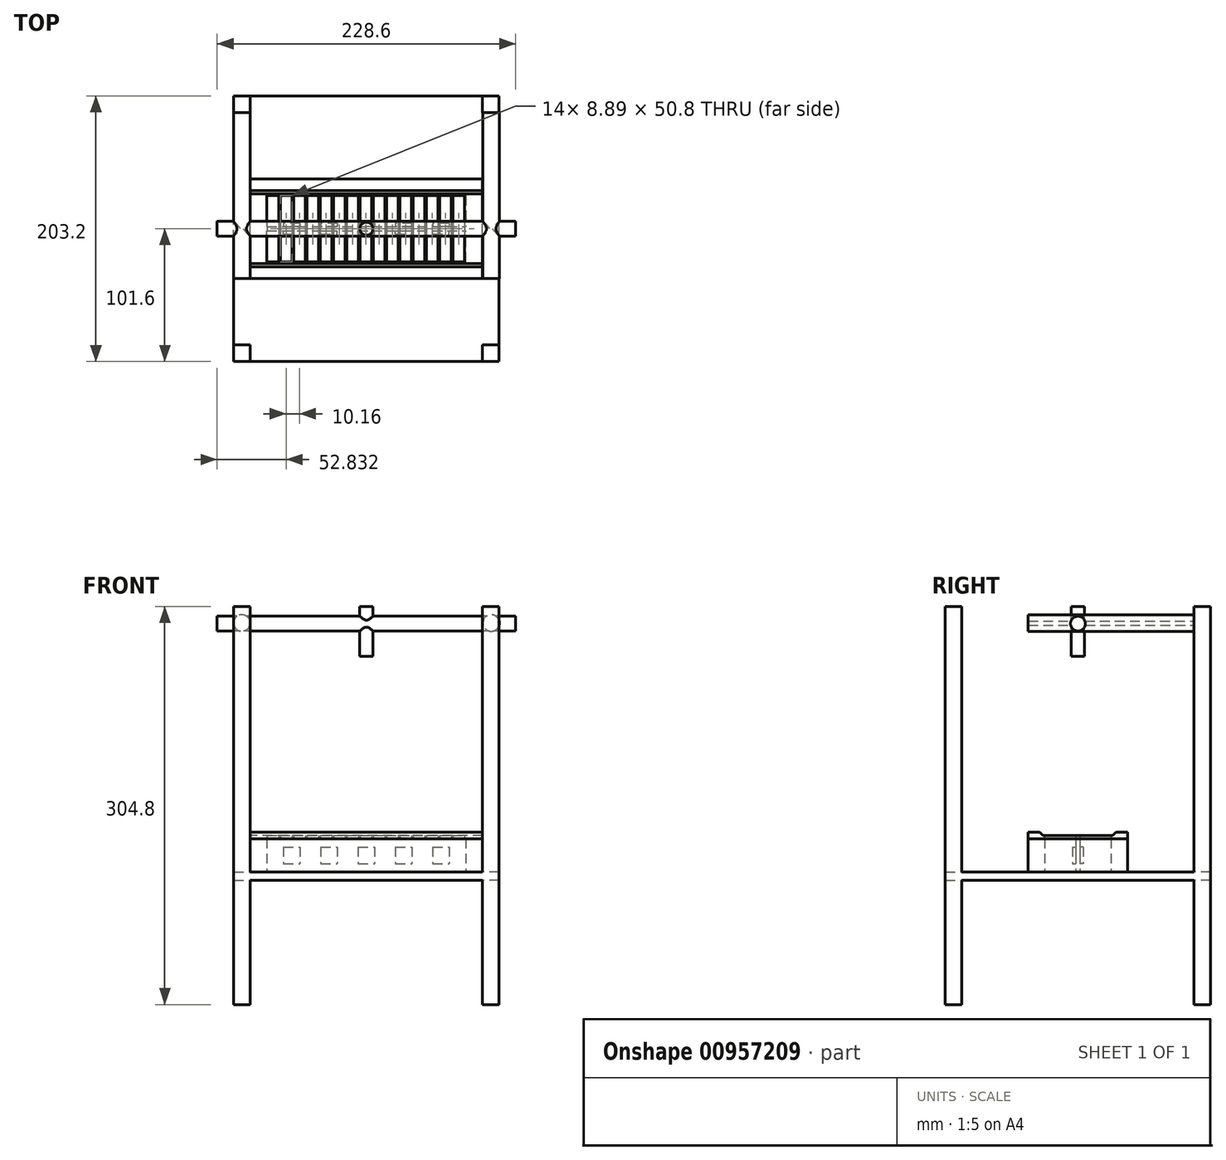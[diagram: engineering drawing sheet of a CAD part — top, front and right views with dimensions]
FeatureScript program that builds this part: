
annotation { "Feature Type Name" : "Feature", "Feature Type Description" : "" }
export const myFeature = defineFeature(function(context is Context, id is Id, definition is map)
    precondition{}
    {
        {
            var Q0;
            Q0=qCreatedBy(makeId("Top.planeOp"),FACE);
            var sketch = newSketch(context, id + "F0", { "sketchPlane" : qUnion([Q0])});
            skLineSegment(sketch, "E0.bottom", {"start": v(88.9, -38.1) * mm, "end": v(-88.9, -38.1) * mm});
            skLineSegment(sketch, "E0.top", {"start": v(88.9, 38.1) * mm, "end": v(-88.9, 38.1) * mm});
            skLineSegment(sketch, "E0.left", {"start": v(88.9, -38.1) * mm, "end": v(88.9, 38.1) * mm});
            skLineSegment(sketch, "E0.right", {"start": v(-88.9, -38.1) * mm, "end": v(-88.9, 38.1) * mm});
            skPoint(sketch, "E0.middle", {"position": v(0, 0) * mm});
            skLineSegment(sketch, "E1.bottom", {"start": v(-76.2, 25.4) * mm, "end": v(76.2, 25.4) * mm});
            skLineSegment(sketch, "E1.top", {"start": v(-76.2, 1.59) * mm, "end": v(76.2, 1.59) * mm});
            skLineSegment(sketch, "E1.left", {"start": v(-76.2, 25.4) * mm, "end": v(-76.2, 1.59) * mm});
            skLineSegment(sketch, "E1.right", {"start": v(76.2, 25.4) * mm, "end": v(76.2, 1.59) * mm});
            skLineSegment(sketch, "E2.bottom", {"start": v(-76.2, -25.4) * mm, "end": v(76.2, -25.4) * mm});
            skLineSegment(sketch, "E2.top", {"start": v(-76.2, -1.59) * mm, "end": v(76.2, -1.59) * mm});
            skLineSegment(sketch, "E2.left", {"start": v(-76.2, -25.4) * mm, "end": v(-76.2, -1.59) * mm});
            skLineSegment(sketch, "E2.right", {"start": v(76.2, -25.4) * mm, "end": v(76.2, -1.59) * mm});
            skSolve(sketch);
        }
        {
            var Q0;
            Q0=makeQuery(id+"F0.imprint","IMPRINT",FACE,{"disambiguationData":[TD([[makeQuery(id+"F0.imprint","IMPRINT",EDGE,{"derivedFrom":sQuery(id+"F0.wireOp",EDGE,"E0.bottom")}),-1.0]])]});
            extrude(context, id + "F1", {"entities" : qUnion([Q0]), "depth" : 25.4 * mm, "offsetDistance" : 25.4 * mm});
        }
        {
            var Q0;
            Q0=makeQuery(id+"F1.opExtrude","CAP_FACE",FACE,{"disambiguationData":[OSD([sQuery(id+"F0.wireOp",EDGE,"E0.bottom"),sQuery(id+"F0.wireOp",EDGE,"E0.top"),sQuery(id+"F0.wireOp",EDGE,"E0.left"),sQuery(id+"F0.wireOp",EDGE,"E0.right"),sQuery(id+"F0.wireOp",EDGE,"E1.bottom"),sQuery(id+"F0.wireOp",EDGE,"E1.top"),sQuery(id+"F0.wireOp",EDGE,"E1.left"),sQuery(id+"F0.wireOp",EDGE,"E1.right"),sQuery(id+"F0.wireOp",EDGE,"E2.bottom"),sQuery(id+"F0.wireOp",EDGE,"E2.top"),sQuery(id+"F0.wireOp",EDGE,"E2.left"),sQuery(id+"F0.wireOp",EDGE,"E2.right")])],"isStart":false});
            var sketch = newSketch(context, id + "F2", { "sketchPlane" : qUnion([Q0])});
            skLineSegment(sketch, "E3.bottom", {"start": v(-88.9, 38.1) * mm, "end": v(88.9, 38.1) * mm});
            skLineSegment(sketch, "E3.top", {"start": v(-88.9, -38.1) * mm, "end": v(88.9, -38.1) * mm});
            skLineSegment(sketch, "E3.left", {"start": v(-88.9, 38.1) * mm, "end": v(-88.9, -38.1) * mm});
            skLineSegment(sketch, "E3.right", {"start": v(88.9, 38.1) * mm, "end": v(88.9, -38.1) * mm});
            skLineSegment(sketch, "E4.bottom", {"start": v(-76.07, 25.4) * mm, "end": v(-67.18, 25.4) * mm});
            skLineSegment(sketch, "E4.top", {"start": v(-76.07, -25.4) * mm, "end": v(-67.18, -25.4) * mm});
            skLineSegment(sketch, "E4.left", {"start": v(-76.07, 25.4) * mm, "end": v(-76.07, -25.4) * mm});
            skLineSegment(sketch, "E4.right", {"start": v(-67.18, 25.4) * mm, "end": v(-67.18, -25.4) * mm});
            skLineSegment(sketch, "E5.bottom", {"start": v(-65.91, 25.4) * mm, "end": v(-57.02, 25.4) * mm});
            skLineSegment(sketch, "E5.top", {"start": v(-65.91, -25.4) * mm, "end": v(-57.02, -25.4) * mm});
            skLineSegment(sketch, "E5.left", {"start": v(-65.91, 25.4) * mm, "end": v(-65.91, -25.4) * mm});
            skLineSegment(sketch, "E5.right", {"start": v(-57.02, 25.4) * mm, "end": v(-57.02, -25.4) * mm});
            skLineSegment(sketch, "E6.bottom", {"start": v(-55.75, 25.4) * mm, "end": v(-46.86, 25.4) * mm});
            skLineSegment(sketch, "E6.top", {"start": v(-55.75, -25.4) * mm, "end": v(-46.86, -25.4) * mm});
            skLineSegment(sketch, "E6.left", {"start": v(-55.75, 25.4) * mm, "end": v(-55.75, -25.4) * mm});
            skLineSegment(sketch, "E6.right", {"start": v(-46.86, 25.4) * mm, "end": v(-46.86, -25.4) * mm});
            skLineSegment(sketch, "E7.bottom", {"start": v(-45.6, 25.4) * mm, "end": v(-36.7, 25.4) * mm});
            skLineSegment(sketch, "E7.top", {"start": v(-45.6, -25.4) * mm, "end": v(-36.7, -25.4) * mm});
            skLineSegment(sketch, "E7.left", {"start": v(-45.6, 25.4) * mm, "end": v(-45.6, -25.4) * mm});
            skLineSegment(sketch, "E7.right", {"start": v(-36.7, 25.4) * mm, "end": v(-36.7, -25.4) * mm});
            skLineSegment(sketch, "E8.bottom", {"start": v(-35.43, 25.4) * mm, "end": v(-26.54, 25.4) * mm});
            skLineSegment(sketch, "E8.top", {"start": v(-35.43, -25.4) * mm, "end": v(-26.54, -25.4) * mm});
            skLineSegment(sketch, "E8.left", {"start": v(-35.43, 25.4) * mm, "end": v(-35.43, -25.4) * mm});
            skLineSegment(sketch, "E8.right", {"start": v(-26.54, 25.4) * mm, "end": v(-26.54, -25.4) * mm});
            skLineSegment(sketch, "E9.bottom", {"start": v(-25.27, 25.4) * mm, "end": v(-16.38, 25.4) * mm});
            skLineSegment(sketch, "E9.top", {"start": v(-25.27, -25.4) * mm, "end": v(-16.38, -25.4) * mm});
            skLineSegment(sketch, "E9.left", {"start": v(-25.27, 25.4) * mm, "end": v(-25.27, -25.4) * mm});
            skLineSegment(sketch, "E9.right", {"start": v(-16.38, 25.4) * mm, "end": v(-16.38, -25.4) * mm});
            skLineSegment(sketch, "E10.bottom", {"start": v(-15.11, 25.4) * mm, "end": v(-6.22, 25.4) * mm});
            skLineSegment(sketch, "E10.top", {"start": v(-15.11, -25.4) * mm, "end": v(-6.22, -25.4) * mm});
            skLineSegment(sketch, "E10.left", {"start": v(-15.11, 25.4) * mm, "end": v(-15.11, -25.4) * mm});
            skLineSegment(sketch, "E10.right", {"start": v(-6.22, 25.4) * mm, "end": v(-6.22, -25.4) * mm});
            skLineSegment(sketch, "E11.bottom", {"start": v(-4.95, 25.4) * mm, "end": v(3.94, 25.4) * mm});
            skLineSegment(sketch, "E11.top", {"start": v(-4.95, -25.4) * mm, "end": v(3.94, -25.4) * mm});
            skLineSegment(sketch, "E11.left", {"start": v(-4.95, 25.4) * mm, "end": v(-4.95, -25.4) * mm});
            skLineSegment(sketch, "E11.right", {"start": v(3.94, 25.4) * mm, "end": v(3.94, -25.4) * mm});
            skLineSegment(sketch, "E12.bottom", {"start": v(5.2, 25.4) * mm, "end": v(14.1, 25.4) * mm});
            skLineSegment(sketch, "E12.top", {"start": v(5.2, -25.4) * mm, "end": v(14.1, -25.4) * mm});
            skLineSegment(sketch, "E12.left", {"start": v(5.2, 25.4) * mm, "end": v(5.2, -25.4) * mm});
            skLineSegment(sketch, "E12.right", {"start": v(14.1, 25.4) * mm, "end": v(14.1, -25.4) * mm});
            skLineSegment(sketch, "E13.bottom", {"start": v(15.37, 25.4) * mm, "end": v(24.26, 25.4) * mm});
            skLineSegment(sketch, "E13.top", {"start": v(15.37, -25.4) * mm, "end": v(24.26, -25.4) * mm});
            skLineSegment(sketch, "E13.left", {"start": v(15.37, 25.4) * mm, "end": v(15.37, -25.4) * mm});
            skLineSegment(sketch, "E13.right", {"start": v(24.26, 25.4) * mm, "end": v(24.26, -25.4) * mm});
            skLineSegment(sketch, "E14.bottom", {"start": v(25.53, 25.4) * mm, "end": v(34.42, 25.4) * mm});
            skLineSegment(sketch, "E14.top", {"start": v(25.53, -25.4) * mm, "end": v(34.42, -25.4) * mm});
            skLineSegment(sketch, "E14.left", {"start": v(25.53, 25.4) * mm, "end": v(25.53, -25.4) * mm});
            skLineSegment(sketch, "E14.right", {"start": v(34.42, 25.4) * mm, "end": v(34.42, -25.4) * mm});
            skLineSegment(sketch, "E15.bottom", {"start": v(35.69, 25.4) * mm, "end": v(44.58, 25.4) * mm});
            skLineSegment(sketch, "E15.top", {"start": v(35.69, -25.4) * mm, "end": v(44.58, -25.4) * mm});
            skLineSegment(sketch, "E15.left", {"start": v(35.69, 25.4) * mm, "end": v(35.69, -25.4) * mm});
            skLineSegment(sketch, "E15.right", {"start": v(44.58, 25.4) * mm, "end": v(44.58, -25.4) * mm});
            skLineSegment(sketch, "E16.bottom", {"start": v(45.85, 25.4) * mm, "end": v(54.74, 25.4) * mm});
            skLineSegment(sketch, "E16.top", {"start": v(45.85, -25.4) * mm, "end": v(54.74, -25.4) * mm});
            skLineSegment(sketch, "E16.left", {"start": v(45.85, 25.4) * mm, "end": v(45.85, -25.4) * mm});
            skLineSegment(sketch, "E16.right", {"start": v(54.74, 25.4) * mm, "end": v(54.74, -25.4) * mm});
            skLineSegment(sketch, "E17.bottom", {"start": v(56, 25.4) * mm, "end": v(64.9, 25.4) * mm});
            skLineSegment(sketch, "E17.top", {"start": v(56, -25.4) * mm, "end": v(64.9, -25.4) * mm});
            skLineSegment(sketch, "E17.left", {"start": v(56, 25.4) * mm, "end": v(56, -25.4) * mm});
            skLineSegment(sketch, "E17.right", {"start": v(64.9, 25.4) * mm, "end": v(64.9, -25.4) * mm});
            skLineSegment(sketch, "E18.bottom", {"start": v(66.17, 25.4) * mm, "end": v(75.06, 25.4) * mm});
            skLineSegment(sketch, "E18.top", {"start": v(66.17, -25.4) * mm, "end": v(75.06, -25.4) * mm});
            skLineSegment(sketch, "E18.left", {"start": v(66.17, 25.4) * mm, "end": v(66.17, -25.4) * mm});
            skLineSegment(sketch, "E18.right", {"start": v(75.06, 25.4) * mm, "end": v(75.06, -25.4) * mm});
            skLineSegment(sketch, "E19", {"start": v(-67.18, 25.4) * mm, "end": v(-65.91, 25.4) * mm});
            skLineSegment(sketch, "E20", {"start": v(-57.02, 25.4) * mm, "end": v(-55.75, 25.4) * mm});
            skLineSegment(sketch, "E21", {"start": v(-46.86, 25.4) * mm, "end": v(-45.6, 25.4) * mm});
            skLineSegment(sketch, "E22", {"start": v(-36.7, 25.4) * mm, "end": v(-35.43, 25.4) * mm});
            skLineSegment(sketch, "E23", {"start": v(-26.54, 25.4) * mm, "end": v(-25.27, 25.4) * mm});
            skLineSegment(sketch, "E24", {"start": v(-16.38, 25.4) * mm, "end": v(-15.11, 25.4) * mm});
            skLineSegment(sketch, "E25", {"start": v(-6.22, 25.4) * mm, "end": v(-4.95, 25.4) * mm});
            skLineSegment(sketch, "E26", {"start": v(3.94, 25.4) * mm, "end": v(5.2, 25.4) * mm});
            skLineSegment(sketch, "E27", {"start": v(14.1, 25.4) * mm, "end": v(15.37, 25.4) * mm});
            skLineSegment(sketch, "E28", {"start": v(24.26, 25.4) * mm, "end": v(25.53, 25.4) * mm});
            skLineSegment(sketch, "E29", {"start": v(34.42, 25.4) * mm, "end": v(35.69, 25.4) * mm});
            skLineSegment(sketch, "E30", {"start": v(44.58, 25.4) * mm, "end": v(45.85, 25.4) * mm});
            skLineSegment(sketch, "E31", {"start": v(54.74, 25.4) * mm, "end": v(56, 25.4) * mm});
            skLineSegment(sketch, "E32", {"start": v(64.9, 25.4) * mm, "end": v(66.17, 25.4) * mm});
            skSolve(sketch);
        }
        {
            var Q0;
            Q0=makeQuery(id+"F2.imprint","IMPRINT",FACE,{"disambiguationData":[TD([[makeQuery(id+"F2.imprint","IMPRINT",EDGE,{"derivedFrom":sQuery(id+"F2.wireOp",EDGE,"E3.bottom")}),1.0]])]});
            var Q1;
            {var subQ0=sQuery(id+"F2.wireOp",EDGE,"E19");Q1=makeQuery(id+"F2.imprint","IMPRINT",FACE,{"disambiguationData":[TD([[makeQuery(id+"F2.imprint","IMPRINT",EDGE,{"derivedFrom":subQ0}),-1.0]])]});}
            var Q2;
            {var subQ0=sQuery(id+"F2.wireOp",EDGE,"E4.right");var subQ1=makeQuery(id+"F1.opExtrude","CAP_EDGE",EDGE,{"disambiguationData":[OSD([sQuery(id+"F0.wireOp",EDGE,"E1.top")])],"isStart":false});var subQ2=makeQuery(id+"F2.imprint","INTERSECT",VERTEX,{"derivedFrom":[subQ1,subQ0]});Q2=makeQuery(id+"F2.imprint","IMPRINT",FACE,{"disambiguationData":[TD([[makeQuery(id+"F2.imprint","IMPRINT",EDGE,{"disambiguationData":[TD([[subQ2,-1.0]])],"derivedFrom":subQ0}),1.0]])]});}
            var Q3;
            {var subQ0=sQuery(id+"F2.wireOp",EDGE,"E4.right");var subQ3=makeQuery(id+"F1.opExtrude","CAP_EDGE",EDGE,{"disambiguationData":[OSD([sQuery(id+"F0.wireOp",EDGE,"E2.top")])],"isStart":false});var subQ4=makeQuery(id+"F2.imprint","INTERSECT",VERTEX,{"derivedFrom":[subQ3,subQ0]});Q3=makeQuery(id+"F2.imprint","IMPRINT",FACE,{"disambiguationData":[TD([[makeQuery(id+"F2.imprint","IMPRINT",EDGE,{"disambiguationData":[TD([[subQ4,-1.0]])],"derivedFrom":subQ3}),-1.0]])]});}
            var Q4;
            {var subQ0=sQuery(id+"F2.wireOp",EDGE,"E20");Q4=makeQuery(id+"F2.imprint","IMPRINT",FACE,{"disambiguationData":[TD([[makeQuery(id+"F2.imprint","IMPRINT",EDGE,{"derivedFrom":subQ0}),-1.0]])]});}
            var Q5;
            {var subQ0=sQuery(id+"F2.wireOp",EDGE,"E5.right");var subQ1=makeQuery(id+"F1.opExtrude","CAP_EDGE",EDGE,{"disambiguationData":[OSD([sQuery(id+"F0.wireOp",EDGE,"E1.top")])],"isStart":false});var subQ2=makeQuery(id+"F2.imprint","INTERSECT",VERTEX,{"derivedFrom":[subQ1,subQ0]});Q5=makeQuery(id+"F2.imprint","IMPRINT",FACE,{"disambiguationData":[TD([[makeQuery(id+"F2.imprint","IMPRINT",EDGE,{"disambiguationData":[TD([[subQ2,-1.0]])],"derivedFrom":subQ0}),1.0]])]});}
            var Q6;
            {var subQ0=sQuery(id+"F2.wireOp",EDGE,"E5.right");var subQ3=makeQuery(id+"F1.opExtrude","CAP_EDGE",EDGE,{"disambiguationData":[OSD([sQuery(id+"F0.wireOp",EDGE,"E2.top")])],"isStart":false});var subQ4=makeQuery(id+"F2.imprint","INTERSECT",VERTEX,{"derivedFrom":[subQ3,subQ0]});Q6=makeQuery(id+"F2.imprint","IMPRINT",FACE,{"disambiguationData":[TD([[makeQuery(id+"F2.imprint","IMPRINT",EDGE,{"disambiguationData":[TD([[subQ4,-1.0]])],"derivedFrom":subQ3}),-1.0]])]});}
            var Q7;
            {var subQ0=sQuery(id+"F2.wireOp",EDGE,"E21");Q7=makeQuery(id+"F2.imprint","IMPRINT",FACE,{"disambiguationData":[TD([[makeQuery(id+"F2.imprint","IMPRINT",EDGE,{"derivedFrom":subQ0}),-1.0]])]});}
            var Q8;
            {var subQ0=sQuery(id+"F2.wireOp",EDGE,"E6.right");var subQ1=makeQuery(id+"F1.opExtrude","CAP_EDGE",EDGE,{"disambiguationData":[OSD([sQuery(id+"F0.wireOp",EDGE,"E1.top")])],"isStart":false});var subQ2=makeQuery(id+"F2.imprint","INTERSECT",VERTEX,{"derivedFrom":[subQ1,subQ0]});Q8=makeQuery(id+"F2.imprint","IMPRINT",FACE,{"disambiguationData":[TD([[makeQuery(id+"F2.imprint","IMPRINT",EDGE,{"disambiguationData":[TD([[subQ2,-1.0]])],"derivedFrom":subQ0}),1.0]])]});}
            var Q9;
            {var subQ0=sQuery(id+"F2.wireOp",EDGE,"E6.right");var subQ3=makeQuery(id+"F1.opExtrude","CAP_EDGE",EDGE,{"disambiguationData":[OSD([sQuery(id+"F0.wireOp",EDGE,"E2.top")])],"isStart":false});var subQ4=makeQuery(id+"F2.imprint","INTERSECT",VERTEX,{"derivedFrom":[subQ3,subQ0]});Q9=makeQuery(id+"F2.imprint","IMPRINT",FACE,{"disambiguationData":[TD([[makeQuery(id+"F2.imprint","IMPRINT",EDGE,{"disambiguationData":[TD([[subQ4,-1.0]])],"derivedFrom":subQ3}),-1.0]])]});}
            var Q10;
            {var subQ0=sQuery(id+"F2.wireOp",EDGE,"E22");Q10=makeQuery(id+"F2.imprint","IMPRINT",FACE,{"disambiguationData":[TD([[makeQuery(id+"F2.imprint","IMPRINT",EDGE,{"derivedFrom":subQ0}),-1.0]])]});}
            var Q11;
            {var subQ0=sQuery(id+"F2.wireOp",EDGE,"E7.right");var subQ1=makeQuery(id+"F1.opExtrude","CAP_EDGE",EDGE,{"disambiguationData":[OSD([sQuery(id+"F0.wireOp",EDGE,"E1.top")])],"isStart":false});var subQ2=makeQuery(id+"F2.imprint","INTERSECT",VERTEX,{"derivedFrom":[subQ1,subQ0]});Q11=makeQuery(id+"F2.imprint","IMPRINT",FACE,{"disambiguationData":[TD([[makeQuery(id+"F2.imprint","IMPRINT",EDGE,{"disambiguationData":[TD([[subQ2,-1.0]])],"derivedFrom":subQ0}),1.0]])]});}
            var Q12;
            {var subQ0=sQuery(id+"F2.wireOp",EDGE,"E7.right");var subQ3=makeQuery(id+"F1.opExtrude","CAP_EDGE",EDGE,{"disambiguationData":[OSD([sQuery(id+"F0.wireOp",EDGE,"E2.top")])],"isStart":false});var subQ4=makeQuery(id+"F2.imprint","INTERSECT",VERTEX,{"derivedFrom":[subQ3,subQ0]});Q12=makeQuery(id+"F2.imprint","IMPRINT",FACE,{"disambiguationData":[TD([[makeQuery(id+"F2.imprint","IMPRINT",EDGE,{"disambiguationData":[TD([[subQ4,-1.0]])],"derivedFrom":subQ3}),-1.0]])]});}
            var Q13;
            {var subQ0=sQuery(id+"F2.wireOp",EDGE,"E23");Q13=makeQuery(id+"F2.imprint","IMPRINT",FACE,{"disambiguationData":[TD([[makeQuery(id+"F2.imprint","IMPRINT",EDGE,{"derivedFrom":subQ0}),-1.0]])]});}
            var Q14;
            {var subQ0=sQuery(id+"F2.wireOp",EDGE,"E8.right");var subQ1=makeQuery(id+"F1.opExtrude","CAP_EDGE",EDGE,{"disambiguationData":[OSD([sQuery(id+"F0.wireOp",EDGE,"E1.top")])],"isStart":false});var subQ2=makeQuery(id+"F2.imprint","INTERSECT",VERTEX,{"derivedFrom":[subQ1,subQ0]});Q14=makeQuery(id+"F2.imprint","IMPRINT",FACE,{"disambiguationData":[TD([[makeQuery(id+"F2.imprint","IMPRINT",EDGE,{"disambiguationData":[TD([[subQ2,-1.0]])],"derivedFrom":subQ0}),1.0]])]});}
            var Q15;
            {var subQ0=sQuery(id+"F2.wireOp",EDGE,"E8.right");var subQ3=makeQuery(id+"F1.opExtrude","CAP_EDGE",EDGE,{"disambiguationData":[OSD([sQuery(id+"F0.wireOp",EDGE,"E2.top")])],"isStart":false});var subQ4=makeQuery(id+"F2.imprint","INTERSECT",VERTEX,{"derivedFrom":[subQ3,subQ0]});Q15=makeQuery(id+"F2.imprint","IMPRINT",FACE,{"disambiguationData":[TD([[makeQuery(id+"F2.imprint","IMPRINT",EDGE,{"disambiguationData":[TD([[subQ4,-1.0]])],"derivedFrom":subQ3}),-1.0]])]});}
            var Q16;
            {var subQ0=sQuery(id+"F2.wireOp",EDGE,"E24");Q16=makeQuery(id+"F2.imprint","IMPRINT",FACE,{"disambiguationData":[TD([[makeQuery(id+"F2.imprint","IMPRINT",EDGE,{"derivedFrom":subQ0}),-1.0]])]});}
            var Q17;
            {var subQ0=sQuery(id+"F2.wireOp",EDGE,"E9.right");var subQ1=makeQuery(id+"F1.opExtrude","CAP_EDGE",EDGE,{"disambiguationData":[OSD([sQuery(id+"F0.wireOp",EDGE,"E1.top")])],"isStart":false});var subQ2=makeQuery(id+"F2.imprint","INTERSECT",VERTEX,{"derivedFrom":[subQ1,subQ0]});Q17=makeQuery(id+"F2.imprint","IMPRINT",FACE,{"disambiguationData":[TD([[makeQuery(id+"F2.imprint","IMPRINT",EDGE,{"disambiguationData":[TD([[subQ2,-1.0]])],"derivedFrom":subQ0}),1.0]])]});}
            var Q18;
            {var subQ0=sQuery(id+"F2.wireOp",EDGE,"E9.right");var subQ3=makeQuery(id+"F1.opExtrude","CAP_EDGE",EDGE,{"disambiguationData":[OSD([sQuery(id+"F0.wireOp",EDGE,"E2.top")])],"isStart":false});var subQ4=makeQuery(id+"F2.imprint","INTERSECT",VERTEX,{"derivedFrom":[subQ3,subQ0]});Q18=makeQuery(id+"F2.imprint","IMPRINT",FACE,{"disambiguationData":[TD([[makeQuery(id+"F2.imprint","IMPRINT",EDGE,{"disambiguationData":[TD([[subQ4,-1.0]])],"derivedFrom":subQ3}),-1.0]])]});}
            var Q19;
            {var subQ0=sQuery(id+"F2.wireOp",EDGE,"E25");Q19=makeQuery(id+"F2.imprint","IMPRINT",FACE,{"disambiguationData":[TD([[makeQuery(id+"F2.imprint","IMPRINT",EDGE,{"derivedFrom":subQ0}),-1.0]])]});}
            var Q20;
            {var subQ0=sQuery(id+"F2.wireOp",EDGE,"E10.right");var subQ1=makeQuery(id+"F1.opExtrude","CAP_EDGE",EDGE,{"disambiguationData":[OSD([sQuery(id+"F0.wireOp",EDGE,"E1.top")])],"isStart":false});var subQ2=makeQuery(id+"F2.imprint","INTERSECT",VERTEX,{"derivedFrom":[subQ1,subQ0]});Q20=makeQuery(id+"F2.imprint","IMPRINT",FACE,{"disambiguationData":[TD([[makeQuery(id+"F2.imprint","IMPRINT",EDGE,{"disambiguationData":[TD([[subQ2,-1.0]])],"derivedFrom":subQ0}),1.0]])]});}
            var Q21;
            {var subQ0=sQuery(id+"F2.wireOp",EDGE,"E10.right");var subQ3=makeQuery(id+"F1.opExtrude","CAP_EDGE",EDGE,{"disambiguationData":[OSD([sQuery(id+"F0.wireOp",EDGE,"E2.top")])],"isStart":false});var subQ4=makeQuery(id+"F2.imprint","INTERSECT",VERTEX,{"derivedFrom":[subQ3,subQ0]});Q21=makeQuery(id+"F2.imprint","IMPRINT",FACE,{"disambiguationData":[TD([[makeQuery(id+"F2.imprint","IMPRINT",EDGE,{"disambiguationData":[TD([[subQ4,-1.0]])],"derivedFrom":subQ3}),-1.0]])]});}
            var Q22;
            {var subQ0=sQuery(id+"F2.wireOp",EDGE,"E26");Q22=makeQuery(id+"F2.imprint","IMPRINT",FACE,{"disambiguationData":[TD([[makeQuery(id+"F2.imprint","IMPRINT",EDGE,{"derivedFrom":subQ0}),-1.0]])]});}
            var Q23;
            {var subQ0=sQuery(id+"F2.wireOp",EDGE,"E11.right");var subQ1=makeQuery(id+"F1.opExtrude","CAP_EDGE",EDGE,{"disambiguationData":[OSD([sQuery(id+"F0.wireOp",EDGE,"E1.top")])],"isStart":false});var subQ2=makeQuery(id+"F2.imprint","INTERSECT",VERTEX,{"derivedFrom":[subQ1,subQ0]});Q23=makeQuery(id+"F2.imprint","IMPRINT",FACE,{"disambiguationData":[TD([[makeQuery(id+"F2.imprint","IMPRINT",EDGE,{"disambiguationData":[TD([[subQ2,-1.0]])],"derivedFrom":subQ0}),1.0]])]});}
            var Q24;
            {var subQ0=sQuery(id+"F2.wireOp",EDGE,"E11.right");var subQ3=makeQuery(id+"F1.opExtrude","CAP_EDGE",EDGE,{"disambiguationData":[OSD([sQuery(id+"F0.wireOp",EDGE,"E2.top")])],"isStart":false});var subQ4=makeQuery(id+"F2.imprint","INTERSECT",VERTEX,{"derivedFrom":[subQ3,subQ0]});Q24=makeQuery(id+"F2.imprint","IMPRINT",FACE,{"disambiguationData":[TD([[makeQuery(id+"F2.imprint","IMPRINT",EDGE,{"disambiguationData":[TD([[subQ4,-1.0]])],"derivedFrom":subQ3}),-1.0]])]});}
            var Q25;
            {var subQ0=sQuery(id+"F2.wireOp",EDGE,"E27");Q25=makeQuery(id+"F2.imprint","IMPRINT",FACE,{"disambiguationData":[TD([[makeQuery(id+"F2.imprint","IMPRINT",EDGE,{"derivedFrom":subQ0}),-1.0]])]});}
            var Q26;
            {var subQ0=sQuery(id+"F2.wireOp",EDGE,"E12.right");var subQ1=makeQuery(id+"F1.opExtrude","CAP_EDGE",EDGE,{"disambiguationData":[OSD([sQuery(id+"F0.wireOp",EDGE,"E1.top")])],"isStart":false});var subQ2=makeQuery(id+"F2.imprint","INTERSECT",VERTEX,{"derivedFrom":[subQ1,subQ0]});Q26=makeQuery(id+"F2.imprint","IMPRINT",FACE,{"disambiguationData":[TD([[makeQuery(id+"F2.imprint","IMPRINT",EDGE,{"disambiguationData":[TD([[subQ2,-1.0]])],"derivedFrom":subQ0}),1.0]])]});}
            var Q27;
            {var subQ0=sQuery(id+"F2.wireOp",EDGE,"E12.right");var subQ3=makeQuery(id+"F1.opExtrude","CAP_EDGE",EDGE,{"disambiguationData":[OSD([sQuery(id+"F0.wireOp",EDGE,"E2.top")])],"isStart":false});var subQ4=makeQuery(id+"F2.imprint","INTERSECT",VERTEX,{"derivedFrom":[subQ3,subQ0]});Q27=makeQuery(id+"F2.imprint","IMPRINT",FACE,{"disambiguationData":[TD([[makeQuery(id+"F2.imprint","IMPRINT",EDGE,{"disambiguationData":[TD([[subQ4,-1.0]])],"derivedFrom":subQ3}),-1.0]])]});}
            var Q28;
            {var subQ0=sQuery(id+"F2.wireOp",EDGE,"E28");Q28=makeQuery(id+"F2.imprint","IMPRINT",FACE,{"disambiguationData":[TD([[makeQuery(id+"F2.imprint","IMPRINT",EDGE,{"derivedFrom":subQ0}),-1.0]])]});}
            var Q29;
            {var subQ0=sQuery(id+"F2.wireOp",EDGE,"E13.right");var subQ1=makeQuery(id+"F1.opExtrude","CAP_EDGE",EDGE,{"disambiguationData":[OSD([sQuery(id+"F0.wireOp",EDGE,"E1.top")])],"isStart":false});var subQ2=makeQuery(id+"F2.imprint","INTERSECT",VERTEX,{"derivedFrom":[subQ1,subQ0]});Q29=makeQuery(id+"F2.imprint","IMPRINT",FACE,{"disambiguationData":[TD([[makeQuery(id+"F2.imprint","IMPRINT",EDGE,{"disambiguationData":[TD([[subQ2,-1.0]])],"derivedFrom":subQ0}),1.0]])]});}
            var Q30;
            {var subQ0=sQuery(id+"F2.wireOp",EDGE,"E13.right");var subQ3=makeQuery(id+"F1.opExtrude","CAP_EDGE",EDGE,{"disambiguationData":[OSD([sQuery(id+"F0.wireOp",EDGE,"E2.top")])],"isStart":false});var subQ4=makeQuery(id+"F2.imprint","INTERSECT",VERTEX,{"derivedFrom":[subQ3,subQ0]});Q30=makeQuery(id+"F2.imprint","IMPRINT",FACE,{"disambiguationData":[TD([[makeQuery(id+"F2.imprint","IMPRINT",EDGE,{"disambiguationData":[TD([[subQ4,-1.0]])],"derivedFrom":subQ3}),-1.0]])]});}
            var Q31;
            {var subQ0=sQuery(id+"F2.wireOp",EDGE,"E29");Q31=makeQuery(id+"F2.imprint","IMPRINT",FACE,{"disambiguationData":[TD([[makeQuery(id+"F2.imprint","IMPRINT",EDGE,{"derivedFrom":subQ0}),-1.0]])]});}
            var Q32;
            {var subQ0=sQuery(id+"F2.wireOp",EDGE,"E14.right");var subQ1=makeQuery(id+"F1.opExtrude","CAP_EDGE",EDGE,{"disambiguationData":[OSD([sQuery(id+"F0.wireOp",EDGE,"E1.top")])],"isStart":false});var subQ2=makeQuery(id+"F2.imprint","INTERSECT",VERTEX,{"derivedFrom":[subQ1,subQ0]});Q32=makeQuery(id+"F2.imprint","IMPRINT",FACE,{"disambiguationData":[TD([[makeQuery(id+"F2.imprint","IMPRINT",EDGE,{"disambiguationData":[TD([[subQ2,-1.0]])],"derivedFrom":subQ0}),1.0]])]});}
            var Q33;
            {var subQ0=sQuery(id+"F2.wireOp",EDGE,"E14.right");var subQ3=makeQuery(id+"F1.opExtrude","CAP_EDGE",EDGE,{"disambiguationData":[OSD([sQuery(id+"F0.wireOp",EDGE,"E2.top")])],"isStart":false});var subQ4=makeQuery(id+"F2.imprint","INTERSECT",VERTEX,{"derivedFrom":[subQ3,subQ0]});Q33=makeQuery(id+"F2.imprint","IMPRINT",FACE,{"disambiguationData":[TD([[makeQuery(id+"F2.imprint","IMPRINT",EDGE,{"disambiguationData":[TD([[subQ4,-1.0]])],"derivedFrom":subQ3}),-1.0]])]});}
            var Q34;
            {var subQ5=makeQuery(id+"F1.opExtrude","CAP_EDGE",EDGE,{"disambiguationData":[OSD([sQuery(id+"F0.wireOp",EDGE,"E1.right")])],"isStart":false});Q34=makeQuery(id+"F2.imprint","IMPRINT",FACE,{"disambiguationData":[TD([[makeQuery(id+"F2.imprint","IMPRINT",EDGE,{"derivedFrom":subQ5}),-1.0]])]});}
            var Q35;
            {var subQ5=makeQuery(id+"F1.opExtrude","CAP_EDGE",EDGE,{"disambiguationData":[OSD([sQuery(id+"F0.wireOp",EDGE,"E2.right")])],"isStart":false});Q35=makeQuery(id+"F2.imprint","IMPRINT",FACE,{"disambiguationData":[TD([[makeQuery(id+"F2.imprint","IMPRINT",EDGE,{"derivedFrom":subQ5}),1.0]])]});}
            var Q36;
            {var subQ0=sQuery(id+"F2.wireOp",EDGE,"E32");Q36=makeQuery(id+"F2.imprint","IMPRINT",FACE,{"disambiguationData":[TD([[makeQuery(id+"F2.imprint","IMPRINT",EDGE,{"derivedFrom":subQ0}),-1.0]])]});}
            var Q37;
            {var subQ0=sQuery(id+"F2.wireOp",EDGE,"E17.right");var subQ1=makeQuery(id+"F1.opExtrude","CAP_EDGE",EDGE,{"disambiguationData":[OSD([sQuery(id+"F0.wireOp",EDGE,"E1.top")])],"isStart":false});var subQ2=makeQuery(id+"F2.imprint","INTERSECT",VERTEX,{"derivedFrom":[subQ1,subQ0]});Q37=makeQuery(id+"F2.imprint","IMPRINT",FACE,{"disambiguationData":[TD([[makeQuery(id+"F2.imprint","IMPRINT",EDGE,{"disambiguationData":[TD([[subQ2,-1.0]])],"derivedFrom":subQ0}),1.0]])]});}
            var Q38;
            {var subQ0=sQuery(id+"F2.wireOp",EDGE,"E17.right");var subQ3=makeQuery(id+"F1.opExtrude","CAP_EDGE",EDGE,{"disambiguationData":[OSD([sQuery(id+"F0.wireOp",EDGE,"E2.top")])],"isStart":false});var subQ4=makeQuery(id+"F2.imprint","INTERSECT",VERTEX,{"derivedFrom":[subQ3,subQ0]});Q38=makeQuery(id+"F2.imprint","IMPRINT",FACE,{"disambiguationData":[TD([[makeQuery(id+"F2.imprint","IMPRINT",EDGE,{"disambiguationData":[TD([[subQ4,-1.0]])],"derivedFrom":subQ3}),-1.0]])]});}
            var Q39;
            {var subQ0=sQuery(id+"F2.wireOp",EDGE,"E31");Q39=makeQuery(id+"F2.imprint","IMPRINT",FACE,{"disambiguationData":[TD([[makeQuery(id+"F2.imprint","IMPRINT",EDGE,{"derivedFrom":subQ0}),-1.0]])]});}
            var Q40;
            {var subQ0=sQuery(id+"F2.wireOp",EDGE,"E16.right");var subQ1=makeQuery(id+"F1.opExtrude","CAP_EDGE",EDGE,{"disambiguationData":[OSD([sQuery(id+"F0.wireOp",EDGE,"E1.top")])],"isStart":false});var subQ2=makeQuery(id+"F2.imprint","INTERSECT",VERTEX,{"derivedFrom":[subQ1,subQ0]});Q40=makeQuery(id+"F2.imprint","IMPRINT",FACE,{"disambiguationData":[TD([[makeQuery(id+"F2.imprint","IMPRINT",EDGE,{"disambiguationData":[TD([[subQ2,-1.0]])],"derivedFrom":subQ0}),1.0]])]});}
            var Q41;
            {var subQ0=sQuery(id+"F2.wireOp",EDGE,"E16.right");var subQ3=makeQuery(id+"F1.opExtrude","CAP_EDGE",EDGE,{"disambiguationData":[OSD([sQuery(id+"F0.wireOp",EDGE,"E2.top")])],"isStart":false});var subQ4=makeQuery(id+"F2.imprint","INTERSECT",VERTEX,{"derivedFrom":[subQ3,subQ0]});Q41=makeQuery(id+"F2.imprint","IMPRINT",FACE,{"disambiguationData":[TD([[makeQuery(id+"F2.imprint","IMPRINT",EDGE,{"disambiguationData":[TD([[subQ4,-1.0]])],"derivedFrom":subQ3}),-1.0]])]});}
            var Q42;
            {var subQ0=sQuery(id+"F2.wireOp",EDGE,"E30");Q42=makeQuery(id+"F2.imprint","IMPRINT",FACE,{"disambiguationData":[TD([[makeQuery(id+"F2.imprint","IMPRINT",EDGE,{"derivedFrom":subQ0}),-1.0]])]});}
            var Q43;
            {var subQ0=sQuery(id+"F2.wireOp",EDGE,"E15.right");var subQ1=makeQuery(id+"F1.opExtrude","CAP_EDGE",EDGE,{"disambiguationData":[OSD([sQuery(id+"F0.wireOp",EDGE,"E1.top")])],"isStart":false});var subQ2=makeQuery(id+"F2.imprint","INTERSECT",VERTEX,{"derivedFrom":[subQ1,subQ0]});Q43=makeQuery(id+"F2.imprint","IMPRINT",FACE,{"disambiguationData":[TD([[makeQuery(id+"F2.imprint","IMPRINT",EDGE,{"disambiguationData":[TD([[subQ2,-1.0]])],"derivedFrom":subQ0}),1.0]])]});}
            var Q44;
            {var subQ0=sQuery(id+"F2.wireOp",EDGE,"E15.right");var subQ3=makeQuery(id+"F1.opExtrude","CAP_EDGE",EDGE,{"disambiguationData":[OSD([sQuery(id+"F0.wireOp",EDGE,"E2.top")])],"isStart":false});var subQ4=makeQuery(id+"F2.imprint","INTERSECT",VERTEX,{"derivedFrom":[subQ3,subQ0]});Q44=makeQuery(id+"F2.imprint","IMPRINT",FACE,{"disambiguationData":[TD([[makeQuery(id+"F2.imprint","IMPRINT",EDGE,{"disambiguationData":[TD([[subQ4,-1.0]])],"derivedFrom":subQ3}),-1.0]])]});}
            extrude(context, id + "F3", {"entities" : qUnion([Q0, Q1, Q2, Q3, Q4, Q5, Q6, Q7, Q8, Q9, Q10, Q11, Q12, Q13, Q14, Q15, Q16, Q17, Q18, Q19, Q20, Q21, Q22, Q23, Q24, Q25, Q26, Q27, Q28, Q29, Q30, Q31, Q32, Q33, Q34, Q35, Q36, Q37, Q38, Q39, Q40, Q41, Q42, Q43, Q44]), "depth" : 2.54 * mm, "offsetDistance" : 25.4 * mm});
        }
        {
            var Q0;
            Q0=makeQuery(id+"F3.opExtrude","CAP_FACE",FACE,{"disambiguationData":[OSD([sQuery(id+"F0.wireOp",EDGE,"E1.bottom"),sQuery(id+"F0.wireOp",EDGE,"E1.top"),sQuery(id+"F0.wireOp",EDGE,"E1.left"),sQuery(id+"F0.wireOp",EDGE,"E2.bottom"),sQuery(id+"F0.wireOp",EDGE,"E2.top"),sQuery(id+"F0.wireOp",EDGE,"E2.left"),sQuery(id+"F2.wireOp",EDGE,"E3.bottom"),sQuery(id+"F2.wireOp",EDGE,"E3.top"),sQuery(id+"F2.wireOp",EDGE,"E3.left"),sQuery(id+"F2.wireOp",EDGE,"E3.right"),sQuery(id+"F2.wireOp",EDGE,"E4.bottom"),sQuery(id+"F2.wireOp",EDGE,"E4.top"),sQuery(id+"F2.wireOp",EDGE,"E4.left"),sQuery(id+"F2.wireOp",EDGE,"E4.right"),sQuery(id+"F2.wireOp",EDGE,"E5.bottom"),sQuery(id+"F2.wireOp",EDGE,"E5.top"),sQuery(id+"F2.wireOp",EDGE,"E5.left"),sQuery(id+"F2.wireOp",EDGE,"E5.right"),sQuery(id+"F2.wireOp",EDGE,"E6.bottom"),sQuery(id+"F2.wireOp",EDGE,"E6.top"),sQuery(id+"F2.wireOp",EDGE,"E6.left"),sQuery(id+"F2.wireOp",EDGE,"E6.right"),sQuery(id+"F2.wireOp",EDGE,"E7.bottom"),sQuery(id+"F2.wireOp",EDGE,"E7.top"),sQuery(id+"F2.wireOp",EDGE,"E7.left"),sQuery(id+"F2.wireOp",EDGE,"E7.right"),sQuery(id+"F2.wireOp",EDGE,"E8.bottom"),sQuery(id+"F2.wireOp",EDGE,"E8.top"),sQuery(id+"F2.wireOp",EDGE,"E8.left"),sQuery(id+"F2.wireOp",EDGE,"E8.right"),sQuery(id+"F2.wireOp",EDGE,"E9.bottom"),sQuery(id+"F2.wireOp",EDGE,"E9.top"),sQuery(id+"F2.wireOp",EDGE,"E9.left"),sQuery(id+"F2.wireOp",EDGE,"E9.right"),sQuery(id+"F2.wireOp",EDGE,"E10.bottom"),sQuery(id+"F2.wireOp",EDGE,"E10.top"),sQuery(id+"F2.wireOp",EDGE,"E10.left"),sQuery(id+"F2.wireOp",EDGE,"E10.right"),sQuery(id+"F2.wireOp",EDGE,"E11.bottom"),sQuery(id+"F2.wireOp",EDGE,"E11.top"),sQuery(id+"F2.wireOp",EDGE,"E11.left"),sQuery(id+"F2.wireOp",EDGE,"E11.right"),sQuery(id+"F2.wireOp",EDGE,"E12.bottom"),sQuery(id+"F2.wireOp",EDGE,"E12.top"),sQuery(id+"F2.wireOp",EDGE,"E12.left"),sQuery(id+"F2.wireOp",EDGE,"E12.right"),sQuery(id+"F2.wireOp",EDGE,"E13.bottom"),sQuery(id+"F2.wireOp",EDGE,"E13.top"),sQuery(id+"F2.wireOp",EDGE,"E13.left"),sQuery(id+"F2.wireOp",EDGE,"E13.right"),sQuery(id+"F2.wireOp",EDGE,"E14.bottom"),sQuery(id+"F2.wireOp",EDGE,"E14.top"),sQuery(id+"F2.wireOp",EDGE,"E14.left"),sQuery(id+"F2.wireOp",EDGE,"E14.right"),sQuery(id+"F2.wireOp",EDGE,"E15.bottom"),sQuery(id+"F2.wireOp",EDGE,"E15.top"),sQuery(id+"F2.wireOp",EDGE,"E15.left"),sQuery(id+"F2.wireOp",EDGE,"E15.right"),sQuery(id+"F2.wireOp",EDGE,"E16.bottom"),sQuery(id+"F2.wireOp",EDGE,"E16.top"),sQuery(id+"F2.wireOp",EDGE,"E16.left"),sQuery(id+"F2.wireOp",EDGE,"E16.right"),sQuery(id+"F2.wireOp",EDGE,"E17.bottom"),sQuery(id+"F2.wireOp",EDGE,"E17.top"),sQuery(id+"F2.wireOp",EDGE,"E17.left"),sQuery(id+"F2.wireOp",EDGE,"E17.right"),sQuery(id+"F2.wireOp",EDGE,"E18.bottom"),sQuery(id+"F2.wireOp",EDGE,"E18.top"),sQuery(id+"F2.wireOp",EDGE,"E18.left"),sQuery(id+"F2.wireOp",EDGE,"E18.right")])],"isStart":false});
            var sketch = newSketch(context, id + "F4", { "sketchPlane" : qUnion([Q0])});
            skLineSegment(sketch, "E33.bottom", {"start": v(-88.9, 38.1) * mm, "end": v(88.9, 38.1) * mm});
            skLineSegment(sketch, "E33.top", {"start": v(-88.9, 26.67) * mm, "end": v(88.9, 26.67) * mm});
            skLineSegment(sketch, "E33.left", {"start": v(-88.9, 38.1) * mm, "end": v(-88.9, 26.67) * mm});
            skLineSegment(sketch, "E33.right", {"start": v(88.9, 38.1) * mm, "end": v(88.9, 26.67) * mm});
            skLineSegment(sketch, "E34.bottom", {"start": v(88.9, -38.1) * mm, "end": v(-88.9, -38.1) * mm});
            skLineSegment(sketch, "E34.top", {"start": v(88.9, -26.67) * mm, "end": v(-88.9, -26.67) * mm});
            skLineSegment(sketch, "E34.left", {"start": v(88.9, -38.1) * mm, "end": v(88.9, -26.67) * mm});
            skLineSegment(sketch, "E34.right", {"start": v(-88.9, -38.1) * mm, "end": v(-88.9, -26.67) * mm});
            skSolve(sketch);
        }
        {
            var Q0;
            Q0=qCreatedBy(makeId("Top.planeOp"),FACE);
            var sketch = newSketch(context, id + "F5", { "sketchPlane" : qUnion([Q0])});
            skLineSegment(sketch, "E35.bottom", {"start": v(101.6, -101.6) * mm, "end": v(-101.6, -101.6) * mm});
            skLineSegment(sketch, "E35.top", {"start": v(101.6, 101.6) * mm, "end": v(-101.6, 101.6) * mm});
            skLineSegment(sketch, "E35.left", {"start": v(101.6, -101.6) * mm, "end": v(101.6, 101.6) * mm});
            skLineSegment(sketch, "E35.right", {"start": v(-101.6, -101.6) * mm, "end": v(-101.6, 101.6) * mm});
            skPoint(sketch, "E35.middle", {"position": v(0, 0) * mm});
            skLineSegment(sketch, "E36.bottom", {"start": v(-101.6, 101.6) * mm, "end": v(-88.9, 101.6) * mm});
            skLineSegment(sketch, "E36.top", {"start": v(-101.6, 88.9) * mm, "end": v(-88.9, 88.9) * mm});
            skLineSegment(sketch, "E36.left", {"start": v(-101.6, 101.6) * mm, "end": v(-101.6, 88.9) * mm});
            skLineSegment(sketch, "E36.right", {"start": v(-88.9, 101.6) * mm, "end": v(-88.9, 88.9) * mm});
            skLineSegment(sketch, "E37.bottom", {"start": v(101.6, 101.6) * mm, "end": v(88.9, 101.6) * mm});
            skLineSegment(sketch, "E37.top", {"start": v(101.6, 88.9) * mm, "end": v(88.9, 88.9) * mm});
            skLineSegment(sketch, "E37.left", {"start": v(101.6, 101.6) * mm, "end": v(101.6, 88.9) * mm});
            skLineSegment(sketch, "E37.right", {"start": v(88.9, 101.6) * mm, "end": v(88.9, 88.9) * mm});
            skLineSegment(sketch, "E38.bottom", {"start": v(101.6, -101.6) * mm, "end": v(88.9, -101.6) * mm});
            skLineSegment(sketch, "E38.top", {"start": v(101.6, -88.9) * mm, "end": v(88.9, -88.9) * mm});
            skLineSegment(sketch, "E38.left", {"start": v(101.6, -101.6) * mm, "end": v(101.6, -88.9) * mm});
            skLineSegment(sketch, "E38.right", {"start": v(88.9, -101.6) * mm, "end": v(88.9, -88.9) * mm});
            skLineSegment(sketch, "E39.bottom", {"start": v(-101.6, -101.6) * mm, "end": v(-88.9, -101.6) * mm});
            skLineSegment(sketch, "E39.top", {"start": v(-101.6, -88.9) * mm, "end": v(-88.9, -88.9) * mm});
            skLineSegment(sketch, "E39.left", {"start": v(-101.6, -101.6) * mm, "end": v(-101.6, -88.9) * mm});
            skLineSegment(sketch, "E39.right", {"start": v(-88.9, -101.6) * mm, "end": v(-88.9, -88.9) * mm});
            skSolve(sketch);
        }
        {
            var Q0;
            {var subQ3=sQuery(id+"F5.wireOp",EDGE,"E36.top");Q0=makeQuery(id+"F5.imprint","IMPRINT",FACE,{"disambiguationData":[TD([[makeQuery(id+"F5.imprint","IMPRINT",EDGE,{"derivedFrom":subQ3}),-1.0]])]});}
            extrude(context, id + "F6", {"entities" : qUnion([Q0]), "oppositeDirection" : true, "depth" : 6.35 * mm, "offsetDistance" : 25.4 * mm});
        }
        {
            var Q0;
            Q0 = qSketchRegion(id + "F4", true);
            extrude(context, id + "F7", {"entities" : qUnion([Q0]), "operationType" : NewBodyOperationType.ADD, "depth" : 2.54 * mm, "offsetDistance" : 25.4 * mm});
        }
        {
            var Q0;
            Q0=makeQuery(id+"F7.opExtrude","CAP_EDGE",EDGE,{"disambiguationData":[OSD([sQuery(id+"F4.wireOp",EDGE,"E33.top")])],"isStart":false});
            var Q1;
            Q1=makeQuery(id+"F7.opExtrude","CAP_EDGE",EDGE,{"disambiguationData":[OSD([sQuery(id+"F4.wireOp",EDGE,"E34.top")])],"isStart":false});
            chamfer(context, id + "F8", {"entities" : qUnion([Q0, Q1]), "width" : 2.54 * mm, "tangentPropagation" : true});
        }
        {
            var Q0;
            {var subQ4=sQuery(id+"F5.wireOp",EDGE,"E36.top");Q0=makeQuery(id+"F5.imprint","IMPRINT",FACE,{"disambiguationData":[TD([[makeQuery(id+"F5.imprint","IMPRINT",EDGE,{"derivedFrom":subQ4}),1.0]])]});}
            var Q1;
            {var subQ4=sQuery(id+"F5.wireOp",EDGE,"E37.top");Q1=makeQuery(id+"F5.imprint","IMPRINT",FACE,{"disambiguationData":[TD([[makeQuery(id+"F5.imprint","IMPRINT",EDGE,{"derivedFrom":subQ4}),-1.0]])]});}
            var Q2;
            {var subQ4=sQuery(id+"F5.wireOp",EDGE,"E38.top");Q2=makeQuery(id+"F5.imprint","IMPRINT",FACE,{"disambiguationData":[TD([[makeQuery(id+"F5.imprint","IMPRINT",EDGE,{"derivedFrom":subQ4}),1.0]])]});}
            var Q3;
            {var subQ4=sQuery(id+"F5.wireOp",EDGE,"E39.top");Q3=makeQuery(id+"F5.imprint","IMPRINT",FACE,{"disambiguationData":[TD([[makeQuery(id+"F5.imprint","IMPRINT",EDGE,{"derivedFrom":subQ4}),-1.0]])]});}
            extrude(context, id + "F9", {"entities" : qUnion([Q0, Q1, Q2, Q3]), "operationType" : NewBodyOperationType.ADD, "oppositeDirection" : true, "depth" : 101.6 * mm, "offsetDistance" : 25.4 * mm});
        }
        {
            var Q0;
            {var subQ4=sQuery(id+"F5.wireOp",EDGE,"E36.top");Q0=makeQuery(id+"F5.imprint","IMPRINT",FACE,{"disambiguationData":[TD([[makeQuery(id+"F5.imprint","IMPRINT",EDGE,{"derivedFrom":subQ4}),1.0]])]});}
            var Q1;
            {var subQ4=sQuery(id+"F5.wireOp",EDGE,"E37.top");Q1=makeQuery(id+"F5.imprint","IMPRINT",FACE,{"disambiguationData":[TD([[makeQuery(id+"F5.imprint","IMPRINT",EDGE,{"derivedFrom":subQ4}),-1.0]])]});}
            var Q2;
            {var subQ4=sQuery(id+"F5.wireOp",EDGE,"E38.top");Q2=makeQuery(id+"F5.imprint","IMPRINT",FACE,{"disambiguationData":[TD([[makeQuery(id+"F5.imprint","IMPRINT",EDGE,{"derivedFrom":subQ4}),1.0]])]});}
            var Q3;
            {var subQ4=sQuery(id+"F5.wireOp",EDGE,"E39.top");Q3=makeQuery(id+"F5.imprint","IMPRINT",FACE,{"disambiguationData":[TD([[makeQuery(id+"F5.imprint","IMPRINT",EDGE,{"derivedFrom":subQ4}),-1.0]])]});}
            extrude(context, id + "F10", {"entities" : qUnion([Q0, Q1, Q2, Q3]), "operationType" : NewBodyOperationType.ADD, "depth" : 203.2 * mm, "offsetDistance" : 25.4 * mm});
        }
        {
            var Q0;
            Q0=makeQuery(id+"F10.opExtrude","SWEPT_FACE",FACE,{"disambiguationData":[OSD([sQuery(id+"F5.wireOp",EDGE,"E36.top")])]});
            var sketch = newSketch(context, id + "F11", { "sketchPlane" : qUnion([Q0])});
            skCircle(sketch, "E40", {"center": v(-95.46, 190.5) * mm, "radius": 6.35 * mm});
            skCircle(sketch, "E41", {"center": v(95.5, 190.5) * mm, "radius": 6.35 * mm});
            skSolve(sketch);
        }
        {
            var Q0;
            {var subQ0=sQuery(id+"F11.wireOp",EDGE,"E40");var subQ1=makeQuery(id+"F10.opExtrude","SWEPT_EDGE",EDGE,{"disambiguationData":[OSD([sQuery(id+"F5.wireOp",EDGE,"E35.right"),sQuery(id+"F5.wireOp",EDGE,"E36.top")])]});var subQ2=makeQuery(id+"F11.imprint","INTERSECT",VERTEX,{"disambiguationData":[OD(0.0)],"derivedFrom":[subQ1,subQ0]});Q0=makeQuery(id+"F11.imprint","IMPRINT",FACE,{"disambiguationData":[TD([[makeQuery(id+"F11.imprint","IMPRINT",EDGE,{"disambiguationData":[TD([[subQ2,1.0]])],"derivedFrom":subQ0}),1.0]])]});}
            var Q1;
            Q1=makeQuery(id+"F11.imprint","IMPRINT",FACE,{"disambiguationData":[TD([[makeQuery(id+"F11.imprint","IMPRINT",EDGE,{"derivedFrom":sQuery(id+"F11.wireOp",EDGE,"E41")}),1.0]])]});
            var Q2;
            Q2=sQuery(id+"F11.wireOp",EDGE,"E40");
            var Q3;
            Q3=sQuery(id+"F11.wireOp",EDGE,"E41");
            extrude(context, id + "F12", {"entities" : qUnion([Q0, Q1]), "operationType" : NewBodyOperationType.ADD, "surfaceOperationType" : NewSurfaceOperationType.ADD, "surfaceEntities" : qUnion([Q2, Q3]), "depth" : 127 * mm, "offsetDistance" : 25.4 * mm});
        }
        {
            var Q0;
            Q0=makeQuery(id+"F10.opExtrude","SWEPT_FACE",FACE,{"disambiguationData":[OSD([sQuery(id+"F5.wireOp",EDGE,"E39.right")])]});
            var sketch = newSketch(context, id + "F13", { "sketchPlane" : qUnion([Q0])});
            skLineSegment(sketch, "E42", {"start": v(-88.9, 179.85) * mm, "end": v(0, 179.85) * mm});
            skLineSegment(sketch, "E43", {"start": v(0, 179.85) * mm, "end": v(0, 190) * mm});
            skCircle(sketch, "E44", {"center": v(0, 190) * mm, "radius": 5.7 * mm});
            skLineSegment(sketch, "E45.bottom", {"start": v(2.82, 176.28) * mm, "end": v(-2.82, 176.28) * mm});
            skLineSegment(sketch, "E45.top", {"start": v(2.82, 183.42) * mm, "end": v(-2.82, 183.42) * mm});
            skLineSegment(sketch, "E45.left", {"start": v(2.82, 176.28) * mm, "end": v(2.82, 183.42) * mm});
            skLineSegment(sketch, "E45.right", {"start": v(-2.82, 176.28) * mm, "end": v(-2.82, 183.42) * mm});
            skPoint(sketch, "E45.middle", {"position": v(0, 179.85) * mm});
            skSolve(sketch);
        }
        {
            var Q0;
            Q0=makeQuery(id+"F13.imprint","IMPRINT",FACE,{"disambiguationData":[TD([[makeQuery(id+"F13.imprint","IMPRINT",EDGE,{"derivedFrom":sQuery(id+"F13.wireOp",EDGE,"E44")}),1.0]])]});
            var Q1;
            Q1=sQuery(id+"F13.wireOp",EDGE,"E44");
            extrude(context, id + "F14", {"entities" : qUnion([Q0]), "operationType" : NewBodyOperationType.ADD, "surfaceEntities" : qUnion([Q1]), "depth" : 203.2 * mm, "offsetDistance" : 25.4 * mm, "hasSecondDirection" : true, "secondDirectionOppositeDirection" : true, "secondDirectionDepth" : 25.4 * mm});
        }
        {
            var Q0;
            Q0=makeQuery(id+"F10.opExtrude","CAP_FACE",FACE,{"disambiguationData":[OSD([sQuery(id+"F5.wireOp",EDGE,"E35.top"),sQuery(id+"F5.wireOp",EDGE,"E35.right"),sQuery(id+"F5.wireOp",EDGE,"E36.top"),sQuery(id+"F5.wireOp",EDGE,"E36.right")])],"isStart":false});
            var sketch = newSketch(context, id + "F15", { "sketchPlane" : qUnion([Q0])});
            skCircle(sketch, "E46", {"center": v(0, 0) * mm, "radius": 5.06 * mm});
            skSolve(sketch);
        }
        {
            var Q0;
            Q0 = qSketchRegion(id + "F15", true);
            extrude(context, id + "F16", {"entities" : qUnion([Q0]), "operationType" : NewBodyOperationType.ADD, "oppositeDirection" : true, "depth" : 38.1 * mm, "offsetDistance" : 25.4 * mm});
        }
        {
            var Q0;
            Q0=makeQuery(id+"F1.opExtrude","SWEPT_FACE",FACE,{"disambiguationData":[OSD([sQuery(id+"F0.wireOp",EDGE,"E2.top")])]});
            var sketch = newSketch(context, id + "F17", { "sketchPlane" : qUnion([Q0])});
            skLineSegment(sketch, "E47.bottom", {"start": v(-63.5, 19.05) * mm, "end": v(-50.8, 19.05) * mm});
            skLineSegment(sketch, "E47.top", {"start": v(-63.5, 6.35) * mm, "end": v(-50.8, 6.35) * mm});
            skLineSegment(sketch, "E47.left", {"start": v(-63.5, 19.05) * mm, "end": v(-63.5, 6.35) * mm});
            skLineSegment(sketch, "E47.right", {"start": v(-50.8, 19.05) * mm, "end": v(-50.8, 6.35) * mm});
            skLineSegment(sketch, "E48.bottom", {"start": v(-34.92, 19.05) * mm, "end": v(-22.22, 19.05) * mm});
            skLineSegment(sketch, "E48.top", {"start": v(-34.92, 6.35) * mm, "end": v(-22.22, 6.35) * mm});
            skLineSegment(sketch, "E48.left", {"start": v(-34.92, 19.05) * mm, "end": v(-34.92, 6.35) * mm});
            skLineSegment(sketch, "E48.right", {"start": v(-22.22, 19.05) * mm, "end": v(-22.22, 6.35) * mm});
            skLineSegment(sketch, "E49.bottom", {"start": v(-6.35, 19.05) * mm, "end": v(6.35, 19.05) * mm});
            skLineSegment(sketch, "E49.top", {"start": v(-6.35, 6.35) * mm, "end": v(6.35, 6.35) * mm});
            skLineSegment(sketch, "E49.left", {"start": v(-6.35, 19.05) * mm, "end": v(-6.35, 6.35) * mm});
            skLineSegment(sketch, "E49.right", {"start": v(6.35, 19.05) * mm, "end": v(6.35, 6.35) * mm});
            skLineSegment(sketch, "E50.bottom", {"start": v(22.23, 19.05) * mm, "end": v(34.93, 19.05) * mm});
            skLineSegment(sketch, "E50.top", {"start": v(22.23, 6.35) * mm, "end": v(34.93, 6.35) * mm});
            skLineSegment(sketch, "E50.left", {"start": v(22.23, 19.05) * mm, "end": v(22.23, 6.35) * mm});
            skLineSegment(sketch, "E50.right", {"start": v(34.93, 19.05) * mm, "end": v(34.93, 6.35) * mm});
            skLineSegment(sketch, "E51.bottom", {"start": v(50.8, 19.05) * mm, "end": v(63.5, 19.05) * mm});
            skLineSegment(sketch, "E51.top", {"start": v(50.8, 6.35) * mm, "end": v(63.5, 6.35) * mm});
            skLineSegment(sketch, "E51.left", {"start": v(50.8, 19.05) * mm, "end": v(50.8, 6.35) * mm});
            skLineSegment(sketch, "E51.right", {"start": v(63.5, 19.05) * mm, "end": v(63.5, 6.35) * mm});
            skLineSegment(sketch, "E52", {"start": v(-50.8, 19.05) * mm, "end": v(-34.92, 19.05) * mm});
            skLineSegment(sketch, "E53", {"start": v(-22.22, 19.05) * mm, "end": v(-6.35, 19.05) * mm});
            skLineSegment(sketch, "E54", {"start": v(6.35, 19.05) * mm, "end": v(22.23, 19.05) * mm});
            skLineSegment(sketch, "E55", {"start": v(34.93, 19.05) * mm, "end": v(50.8, 19.05) * mm});
            skSolve(sketch);
        }
        {
            var Q0;
            Q0=makeQuery(id+"F1.opExtrude","SWEPT_FACE",FACE,{"disambiguationData":[OSD([sQuery(id+"F0.wireOp",EDGE,"E1.top")])]});
            var sketch = newSketch(context, id + "F18", { "sketchPlane" : qUnion([Q0])});
            skLineSegment(sketch, "E56.bottom", {"start": v(-63.5, 19.05) * mm, "end": v(-50.8, 19.05) * mm});
            skLineSegment(sketch, "E56.top", {"start": v(-63.5, 6.35) * mm, "end": v(-50.8, 6.35) * mm});
            skLineSegment(sketch, "E56.left", {"start": v(-63.5, 19.05) * mm, "end": v(-63.5, 6.35) * mm});
            skLineSegment(sketch, "E56.right", {"start": v(-50.8, 19.05) * mm, "end": v(-50.8, 6.35) * mm});
            skLineSegment(sketch, "E57.bottom", {"start": v(-34.93, 19.05) * mm, "end": v(-22.23, 19.05) * mm});
            skLineSegment(sketch, "E57.top", {"start": v(-34.93, 6.35) * mm, "end": v(-22.23, 6.35) * mm});
            skLineSegment(sketch, "E57.left", {"start": v(-34.93, 19.05) * mm, "end": v(-34.93, 6.35) * mm});
            skLineSegment(sketch, "E57.right", {"start": v(-22.23, 19.05) * mm, "end": v(-22.23, 6.35) * mm});
            skLineSegment(sketch, "E58.bottom", {"start": v(-6.35, 19.05) * mm, "end": v(6.35, 19.05) * mm});
            skLineSegment(sketch, "E58.top", {"start": v(-6.35, 6.35) * mm, "end": v(6.35, 6.35) * mm});
            skLineSegment(sketch, "E58.left", {"start": v(-6.35, 19.05) * mm, "end": v(-6.35, 6.35) * mm});
            skLineSegment(sketch, "E58.right", {"start": v(6.35, 19.05) * mm, "end": v(6.35, 6.35) * mm});
            skLineSegment(sketch, "E59.bottom", {"start": v(22.22, 19.05) * mm, "end": v(34.92, 19.05) * mm});
            skLineSegment(sketch, "E59.top", {"start": v(22.22, 6.35) * mm, "end": v(34.92, 6.35) * mm});
            skLineSegment(sketch, "E59.left", {"start": v(22.22, 19.05) * mm, "end": v(22.22, 6.35) * mm});
            skLineSegment(sketch, "E59.right", {"start": v(34.92, 19.05) * mm, "end": v(34.92, 6.35) * mm});
            skLineSegment(sketch, "E60.bottom", {"start": v(50.8, 19.05) * mm, "end": v(63.5, 19.05) * mm});
            skLineSegment(sketch, "E60.top", {"start": v(50.8, 6.35) * mm, "end": v(63.5, 6.35) * mm});
            skLineSegment(sketch, "E60.left", {"start": v(50.8, 19.05) * mm, "end": v(50.8, 6.35) * mm});
            skLineSegment(sketch, "E60.right", {"start": v(63.5, 19.05) * mm, "end": v(63.5, 6.35) * mm});
            skLineSegment(sketch, "E61", {"start": v(-50.8, 19.05) * mm, "end": v(-34.93, 19.05) * mm});
            skLineSegment(sketch, "E62", {"start": v(-22.23, 19.05) * mm, "end": v(-6.35, 19.05) * mm});
            skLineSegment(sketch, "E63", {"start": v(6.35, 19.05) * mm, "end": v(22.22, 19.05) * mm});
            skLineSegment(sketch, "E64", {"start": v(34.92, 19.05) * mm, "end": v(50.8, 19.05) * mm});
            skSolve(sketch);
        }
        {
            var Q0;
            Q0 = qSketchRegion(id + "F17", true);
            extrude(context, id + "F19", {"entities" : qUnion([Q0]), "operationType" : NewBodyOperationType.ADD, "depth" : 2.54 * mm, "offsetDistance" : 25.4 * mm});
        }
        {
            var Q0;
            Q0 = qSketchRegion(id + "F18", true);
            extrude(context, id + "F20", {"entities" : qUnion([Q0]), "operationType" : NewBodyOperationType.ADD, "depth" : 2.54 * mm, "offsetDistance" : 25.4 * mm});
        }
    });
